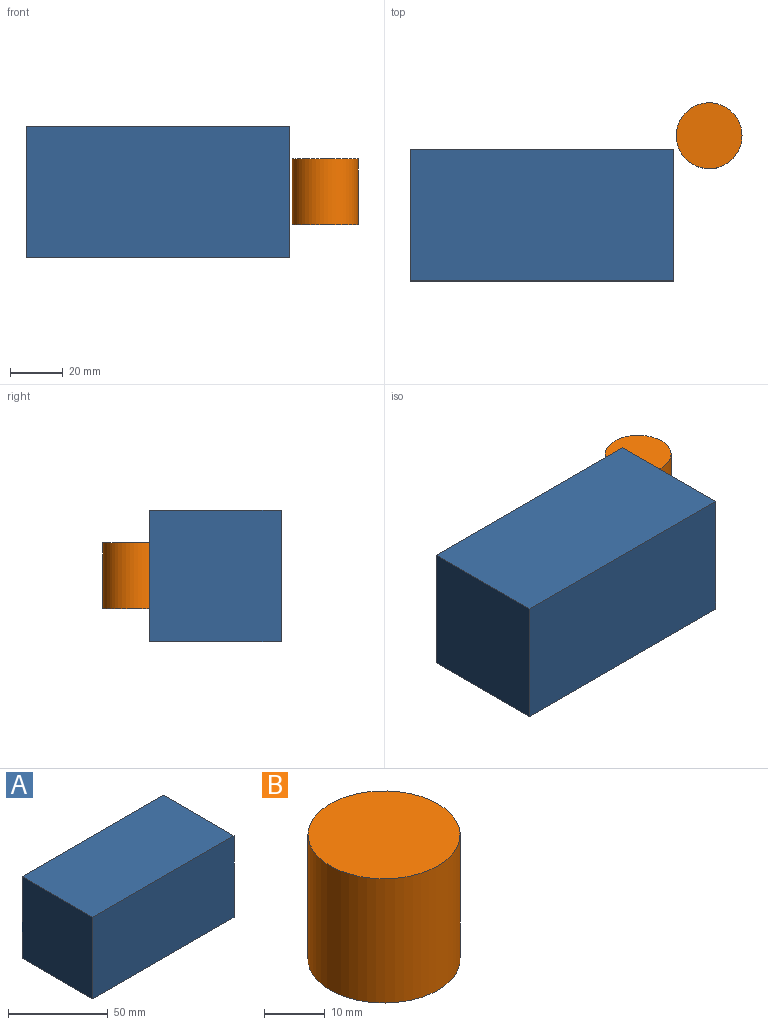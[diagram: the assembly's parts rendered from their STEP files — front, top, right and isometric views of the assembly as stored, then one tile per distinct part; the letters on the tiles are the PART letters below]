
ASSEMBLY  parts=2 mates=1
PART A: 6 faces, bbox 100x50x50 mm
  f0: plane 100x50mm, normal (0,-1,0), area 5000mm2, adj f1,f3,f4,f5
  f1: plane 50x50mm, normal (1,0,0), area 2500mm2, adj f0,f2,f4,f5
  f2: plane 100x50mm, normal (0,1,0), area 5000mm2, adj f1,f3,f4,f5
  f3: plane 50x50mm, normal (-1,0,0), area 2500mm2, adj f0,f2,f4,f5
  f4: plane 100x50mm, normal (0,0,-1), area 5000mm2, adj f0,f1,f2,f3
  f5: plane 100x50mm, normal (0,0,1), area 5000mm2, adj f0,f1,f2,f3
PART B: 3 faces, bbox 25x25x25 mm
  f0: cylinder r=12.5mm len=25mm, axis (0,0,-1), area 1963.5mm2, adj f1,f2
  f1: plane 25x25mm, normal (0,0,1), area 490.9mm2, adj f0
  f2: plane 25x25mm, normal (0,0,-1), area 490.9mm2, adj f0
PLACE A t=(-19.93,-20.91,10.89)mm fixed
PLACE B rot(axis=(0,0,1),0deg) t=(43.54,9.21,-26.53)mm
MATE parallel B.f0 <-> A.f4  axis (0,0,-1) through (43.54,9.21,-26.53)mm
